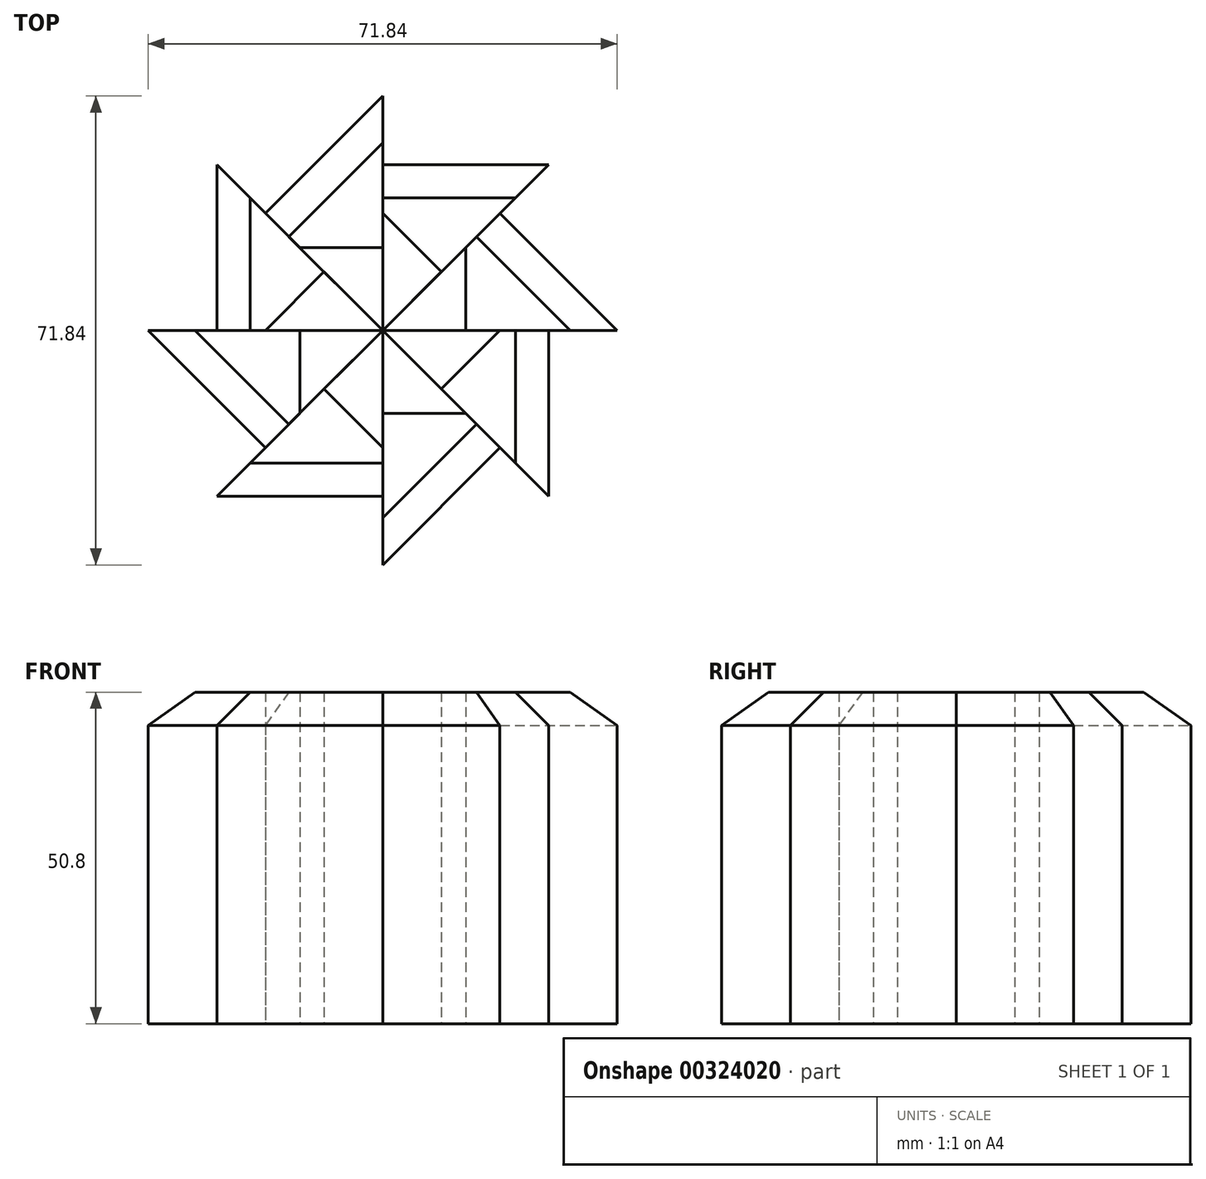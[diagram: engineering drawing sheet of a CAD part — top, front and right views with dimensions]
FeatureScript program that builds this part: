
annotation { "Feature Type Name" : "Feature", "Feature Type Description" : "" }
export const myFeature = defineFeature(function(context is Context, id is Id, definition is map)
    precondition{}
    {
        {
            var Q0;
            Q0=qCreatedBy(makeId("Top.planeOp"),FACE);
            var sketch = newSketch(context, id + "F0", { "sketchPlane" : qUnion([Q0])});
            skLineSegment(sketch, "E0", {"start": v(-25.4, 25.4) * mm, "end": v(-25.4, 0) * mm});
            skLineSegment(sketch, "E1", {"start": v(-25.4, 0) * mm, "end": v(0, 0) * mm});
            skLineSegment(sketch, "E2", {"start": v(0, 0) * mm, "end": v(0, 12.7) * mm});
            skPoint(sketch, "E2.endSnap0", {"position": v(-25.4, 12.7) * mm});
            skLineSegment(sketch, "E3", {"start": v(0, 12.7) * mm, "end": v(-12.7, 12.7) * mm});
            skPoint(sketch, "E3.endSnap0", {"position": v(-12.7, 0) * mm});
            skLineSegment(sketch, "E4", {"start": v(-12.7, 12.7) * mm, "end": v(-25.4, 25.4) * mm});
            skSolve(sketch);
        }
        {
            var Q0;
            Q0=makeQuery(id+"F0.imprint","IMPRINT",FACE,{"disambiguationData":[TD([[makeQuery(id+"F0.imprint","IMPRINT",EDGE,{"derivedFrom":sQuery(id+"F0.wireOp",EDGE,"E0")}),1.0]])]});
            extrude(context, id + "F1", {"entities" : qUnion([Q0]), "depth" : 25.4 * mm, "hasSecondDirection" : true, "secondDirectionOppositeDirection" : true, "secondDirectionDepth" : 25.4 * mm});
        }
        {
            var Q0;
            Q0=makeQuery(id+"F1.opExtrude","SWEPT_BODY",BODY,{"disambiguationData":[OSD([sQuery(id+"F0.wireOp",EDGE,"E0"),sQuery(id+"F0.wireOp",EDGE,"E1"),sQuery(id+"F0.wireOp",EDGE,"E2"),sQuery(id+"F0.wireOp",EDGE,"E3"),sQuery(id+"F0.wireOp",EDGE,"E4")])]});
            var Q1;
            Q1=makeQuery(id+"F1.opExtrude","SWEPT_EDGE",EDGE,{"disambiguationData":[OSD([sQuery(id+"F0.wireOp",EDGE,"E1"),sQuery(id+"F0.wireOp",EDGE,"E2")])]});
            circularPattern(context, id + "F2", {"entities" : qUnion([Q0]), "axis" : qUnion([Q1]), "angle" : 360 * degree, "instanceCount" : 8, "equalSpace" : true});
        }
        {
            var Q0;
            Q0=makeQuery(id+"F2.opPattern","COPY",EDGE,{"derivedFrom":makeQuery(id+"F1.opExtrude","CAP_EDGE",EDGE,{"disambiguationData":[OSD([sQuery(id+"F0.wireOp",EDGE,"E0")])],"isStart":false}),"instanceName":"5"});
            var Q1;
            Q1=makeQuery(id+"F2.opPattern","COPY",EDGE,{"derivedFrom":makeQuery(id+"F1.opExtrude","CAP_EDGE",EDGE,{"disambiguationData":[OSD([sQuery(id+"F0.wireOp",EDGE,"E0")])],"isStart":false}),"instanceName":"6"});
            var Q2;
            Q2=makeQuery(id+"F2.opPattern","COPY",EDGE,{"derivedFrom":makeQuery(id+"F1.opExtrude","CAP_EDGE",EDGE,{"disambiguationData":[OSD([sQuery(id+"F0.wireOp",EDGE,"E0")])],"isStart":false}),"instanceName":"7"});
            var Q3;
            Q3=makeQuery(id+"F1.opExtrude","CAP_EDGE",EDGE,{"disambiguationData":[OSD([sQuery(id+"F0.wireOp",EDGE,"E0")])],"isStart":false});
            var Q4;
            Q4=makeQuery(id+"F2.opPattern","COPY",EDGE,{"derivedFrom":makeQuery(id+"F1.opExtrude","CAP_EDGE",EDGE,{"disambiguationData":[OSD([sQuery(id+"F0.wireOp",EDGE,"E0")])],"isStart":false}),"instanceName":"1"});
            var Q5;
            Q5=makeQuery(id+"F2.opPattern","COPY",EDGE,{"derivedFrom":makeQuery(id+"F1.opExtrude","CAP_EDGE",EDGE,{"disambiguationData":[OSD([sQuery(id+"F0.wireOp",EDGE,"E0")])],"isStart":false}),"instanceName":"2"});
            var Q6;
            Q6=makeQuery(id+"F2.opPattern","COPY",EDGE,{"derivedFrom":makeQuery(id+"F1.opExtrude","CAP_EDGE",EDGE,{"disambiguationData":[OSD([sQuery(id+"F0.wireOp",EDGE,"E0")])],"isStart":false}),"instanceName":"3"});
            var Q7;
            Q7=makeQuery(id+"F2.opPattern","COPY",EDGE,{"derivedFrom":makeQuery(id+"F1.opExtrude","CAP_EDGE",EDGE,{"disambiguationData":[OSD([sQuery(id+"F0.wireOp",EDGE,"E0")])],"isStart":false}),"instanceName":"4"});
            chamfer(context, id + "F3", {"entities" : qUnion([Q0, Q1, Q2, Q3, Q4, Q5, Q6, Q7]), "width" : 5.08 * mm, "tangentPropagation" : true});
        }
    });
